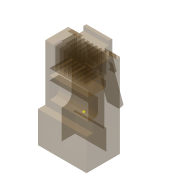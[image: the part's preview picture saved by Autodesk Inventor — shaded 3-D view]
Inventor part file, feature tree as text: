
AUTODESK INVENTOR PART (.ipt)
format: ipt  version: 2022 (Build 260153000, 153)  size: 442,368 bytes
history: native  units: mm
features: extrude x13, sketch x13, projected_geometry x7, fillet x5, plane x1
ambient origin geometry x8: Origin, YZ Plane, XZ Plane, XY Plane, X Axis, Y Axis, Z Axis, Center Point
bodies: Solid1 (feature_tree)
feature tree (39):
  extrude  "Extrusion1"  Depth=6.5mm
  extrude  "Extrusion2"  Depth=6.1mm
  plane  "Work Plane1"
  extrude  "Extrusion3"  Depth=2.75mm
  extrude  "Extrusion4"  Depth=1.0mm
  fillet  "Fillet1"  [1 undecoded]
  fillet  "Fillet2"  Radius=0.5mm
  extrude  "Extrusion5"  Depth=6.1mm
  extrude  "Extrusion6"  Depth=6.1mm
  extrude  "Extrusion7"  Depth=1.3mm
  extrude  "Extrusion8"  Depth=1.0mm
  extrude  "Extrusion9"  Depth=1.0mm
  extrude  "Extrusion10"  Depth=10.0mm TaperAngle=0.0deg
  extrude  "Extrusion11"  Depth=10.0mm
  fillet  "Fillet3"  Radius=0.5mm
  extrude  "Extrusion12"  Depth=0.5mm
  extrude  "Extrusion13"  Depth=0.3mm
  fillet  "Fillet4"  Radius=0.5mm
  fillet  "Fillet5"  Radius=2.0mm
  sketch  "Sketch1"  dims[d0=11.6mm d1=6.5mm]
  sketch  "Sketch2"  dims[d2=21.0mm d3=0.0mm d4=6.1mm]
  sketch  "Sketch3"  dims[d5=11.6mm d6=2.75mm]
  sketch  "Sketch4"  dims[d7=1.0mm d8=2.4mm d9=0.0mm d10=0.0mm d14=6.1mm d16=75.0deg d17=0.5mm]
  sketch  "Sketch5"  dims[d18=4.0mm d19=0.75mm d20=0.0mm d21=0.0mm d22=6.1mm]
  sketch  "Sketch6"  dims[d23=3.1mm d25=6.1mm]
  sketch  "Sketch7"  dims[d27=1.3mm d28=0.5mm]
  sketch  "Sketch8"  dims[d29=10.0mm d30=1.0mm d31=0.0mm d32=0.0mm d33=1.0mm]
  sketch  "Sketch9"  dims[d34=0.2mm d35=1.0mm]
  sketch  "Sketch10"  dims[d36=1.0mm d37=10.0mm d38=0.0mm]
  sketch  "Sketch11"  dims[d39=10.0mm d40=0.0mm d43=0.5mm d44=0.5mm]
  sketch  "Sketch12"  dims[d45=0.5mm d46=0.5mm]
  sketch  "Sketch13"  dims[d47=2.0mm d48=0.5mm d49=0.5mm d50=2.0mm d51=0.5mm d52=0.5mm d53=2.0mm d54=0.5mm d55=0.5mm d56=2.0mm d57=0.5mm d58=0.5mm d59=2.0mm d60=0.5mm d61=0.5mm d62=2.0mm d63=0.5mm d65=2.05mm d66=5.0mm d67=0.0mm d68=9.3mm d69=1.5mm d70=0.95mm d71=11.2mm d72=0.3mm d73=4.2mm d74=0.0mm d75=1.0mm d76=2.3mm d77=4.0mm d78=1.0mm d79=4.2mm d80=0.0mm d81=13.5mm d82=1.6mm d83=2.1mm d84=0.0mm d85=0.0mm d86=2.0mm d87=3.4mm d88=0.0mm d89=1.95mm d90=1.6mm d91=0.0mm d92=0.2mm d93=3.2mm d94=0.0mm d95=0.3mm d96=0.3mm]
  projected_geometry  "Projected Loop1"
  projected_geometry  "Projected Loop2"
  projected_geometry  "Projected Loop3"
  projected_geometry  "Projected Loop4"
  projected_geometry  "Projected Loop5"
  projected_geometry  "Projected Loop6"
  projected_geometry  "Projected Loop7"
note: 1 required parameter value undecoded (feature->parameter linkage not recoverable at this tier; creation-order binding heuristic only, values carry confidence <= 0.55)
